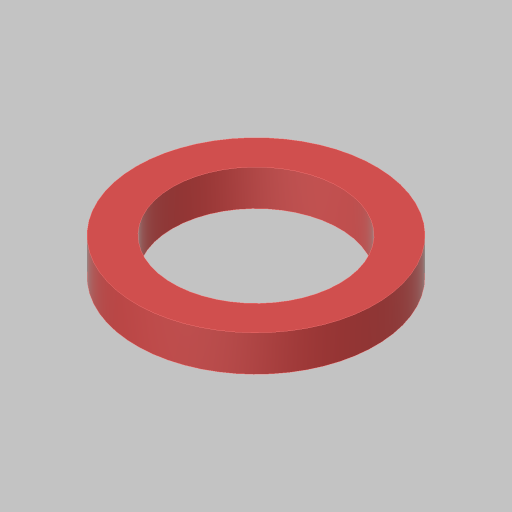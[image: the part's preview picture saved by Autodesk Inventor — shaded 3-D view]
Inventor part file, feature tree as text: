
AUTODESK INVENTOR PART (.ipt)
format: ipt  version: 2023.5 (Build 275446000, 446)  size: 100,864 bytes
history: native  units: in
note: dims shown in document units (in); Inventor stores cm internally (conversion verified against a paired STEP export)
features: extrude x1, sketch x1
ambient origin geometry x8: Origin, YZ Plane, XZ Plane, XY Plane, X Axis, Y Axis, Z Axis, Center Point
bodies: Solid1 (feature_tree)
feature tree (2):
  extrude  "Extrusion1"  Depth=0.125in
  sketch  "Sketch1"  dims[d0=0.58in d1=0.125in d2=0.125in d3=0.0in]
